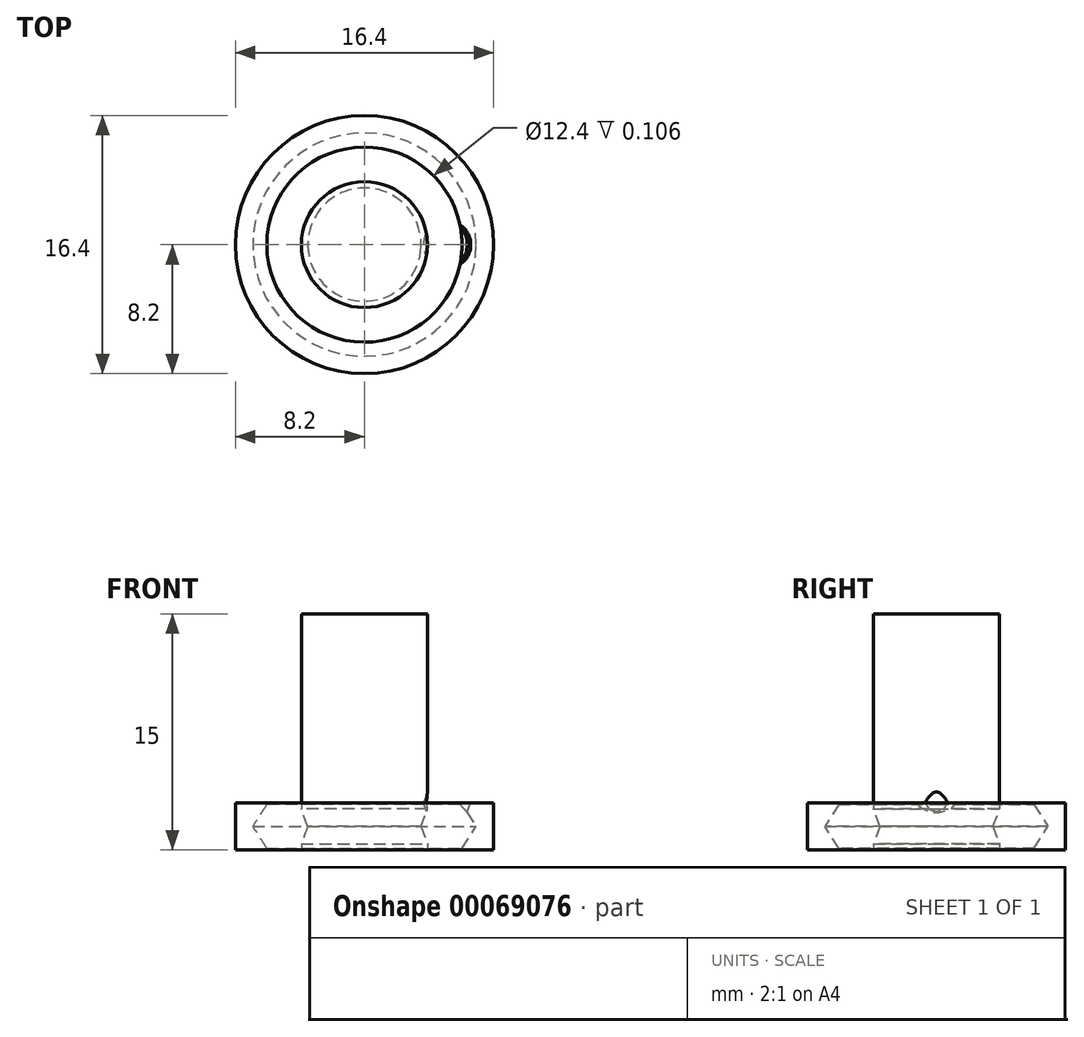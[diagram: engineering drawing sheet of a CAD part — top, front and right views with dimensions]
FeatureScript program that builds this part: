
annotation { "Feature Type Name" : "Feature", "Feature Type Description" : "" }
export const myFeature = defineFeature(function(context is Context, id is Id, definition is map)
    precondition{}
    {
        {
            var Q0;
            Q0=qCreatedBy(makeId("Front.planeOp"),FACE);
            var sketch = newSketch(context, id + "F0", { "sketchPlane" : qUnion([Q0])});
            skLineSegment(sketch, "E0.bottom", {"start": v(0, 0) * mm, "end": v(4, 0) * mm});
            skLineSegment(sketch, "E0.top", {"start": v(0, 15) * mm, "end": v(4, 15) * mm});
            skLineSegment(sketch, "E0.left", {"start": v(0, 0) * mm, "end": v(0, 15) * mm});
            skLineSegment(sketch, "E0.right", {"start": v(4, 0) * mm, "end": v(4, 15) * mm});
            skLineSegment(sketch, "E1.bottom", {"start": v(6.2, 3) * mm, "end": v(8.2, 3) * mm});
            skLineSegment(sketch, "E1.top", {"start": v(6.2, 0) * mm, "end": v(8.2, 0) * mm});
            skLineSegment(sketch, "E1.left", {"start": v(6.2, 3) * mm, "end": v(6.2, 0) * mm});
            skLineSegment(sketch, "E1.right", {"start": v(8.2, 3) * mm, "end": v(8.2, 0) * mm});
            skCircle(sketch, "E2", {"center": v(5.25, 1.5) * mm, "radius": 1.55 * mm});
            skLineSegment(sketch, "E3", {"start": v(6.2, 1.5) * mm, "end": v(4, 1.5) * mm, "construction": true});
            skLineSegment(sketch, "E4", {"start": v(7.09, 1.5) * mm, "end": v(6.2, 2.9) * mm});
            skLineSegment(sketch, "E5.MirrorCS", {"start": v(7.09, 1.5) * mm, "end": v(6.2, 0.1) * mm});
            skLineSegment(sketch, "E6", {"start": v(3.6, 1.5) * mm, "end": v(4, 2.6) * mm});
            skLineSegment(sketch, "E7.MirrorCS", {"start": v(3.6, 1.5) * mm, "end": v(4, 0.4) * mm});
            skSolve(sketch);
        }
        {
            var Q0;
            {var subQ1=sQuery(id+"F0.wireOp",EDGE,"E0.bottom");Q0=makeQuery(id+"F0.imprint","IMPRINT",FACE,{"disambiguationData":[TD([[makeQuery(id+"F0.imprint","IMPRINT",EDGE,{"derivedFrom":subQ1}),1.0]])]});}
            var Q1;
            {var subQ4=sQuery(id+"F0.wireOp",EDGE,"E1.bottom");Q1=makeQuery(id+"F0.imprint","IMPRINT",FACE,{"disambiguationData":[TD([[makeQuery(id+"F0.imprint","IMPRINT",EDGE,{"derivedFrom":subQ4}),-1.0]])]});}
            var Q2;
            Q2=sQuery(id+"F0.wireOp",EDGE,"E0.left");
            revolve(context, id + "F1", {"entities" : qUnion([Q0, Q1]), "axis" : qUnion([Q2]), "revolveType" : RevolveType.FULL});
        }
        {
            var Q0;
            Q0=makeQuery(id+"F1.opRevolve","SWEPT_FACE",FACE,{"disambiguationData":[OSD([sQuery(id+"F0.wireOp",EDGE,"E1.bottom")])]});
            var sketch = newSketch(context, id + "F2", { "sketchPlane" : qUnion([Q0])});
            skCircle(sketch, "E8", {"center": v(5.25, 0) * mm, "radius": 1.5 * mm});
            skSolve(sketch);
        }
        {
            var Q0;
            Q0 = qSketchRegion(id + "F2", true);
            extrude(context, id + "F3", {"entities" : qUnion([Q0]), "operationType" : NewBodyOperationType.REMOVE, "endBound" : BoundingType.SYMMETRIC, "oppositeDirection" : true, "depth" : 3 * mm, "hasDraft" : true, "draftAngle" : 20 * degree, "draftPullDirection" : true});
        }
    });
